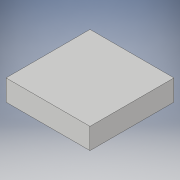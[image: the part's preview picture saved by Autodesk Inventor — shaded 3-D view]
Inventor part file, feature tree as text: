
AUTODESK INVENTOR PART (.ipt)
format: ipt  version: 2019 (Build 230136000, 136)  size: 88,064 bytes
history: native  units: mm
features: extrude x1, sketch x1
ambient origin geometry x8: Origin, YZ Plane, XZ Plane, XY Plane, X Axis, Y Axis, Z Axis, Center Point
bodies: Solid1 (feature_tree)
feature tree (2):
  extrude  "Extrusion1"  Depth=20.0mm
  sketch  "Sketch1"  dims[d0=20.0mm d1=20.0mm d2=5.0mm d3=0.0mm]
